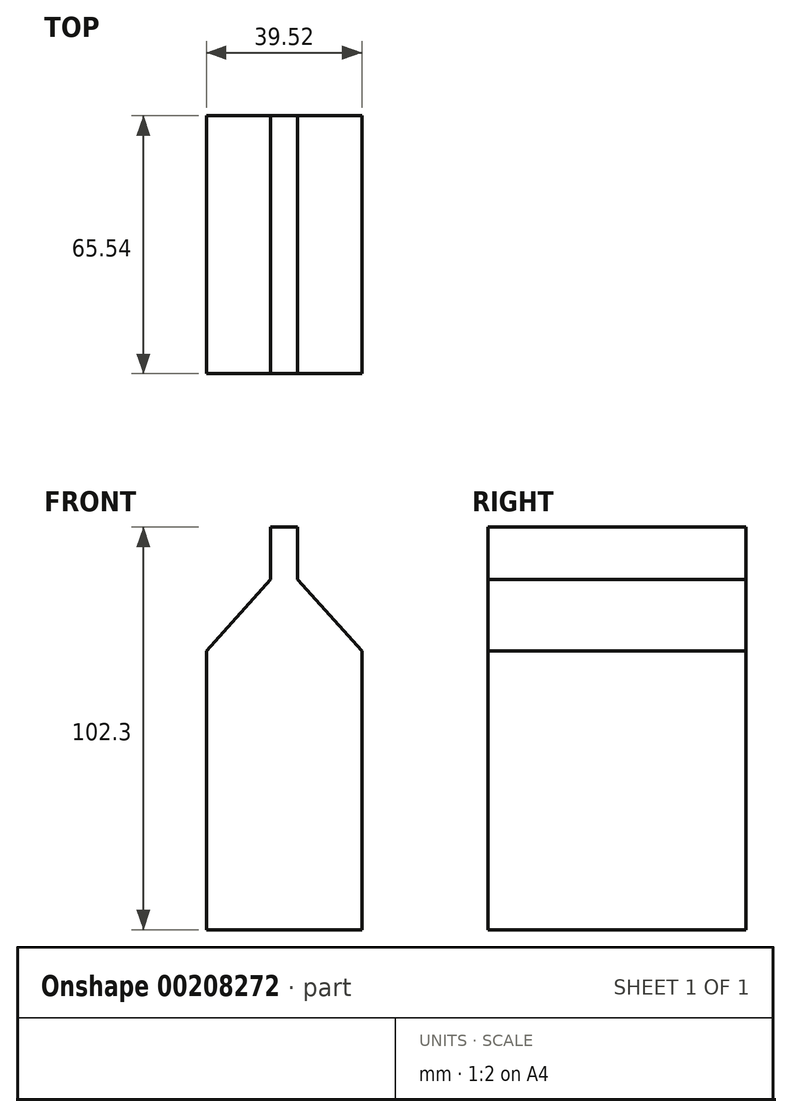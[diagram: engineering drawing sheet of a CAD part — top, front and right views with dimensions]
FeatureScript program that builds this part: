
annotation { "Feature Type Name" : "Feature", "Feature Type Description" : "" }
export const myFeature = defineFeature(function(context is Context, id is Id, definition is map)
    precondition{}
    {
        {
            var Q0;
            Q0=qCreatedBy(makeId("Front.planeOp"),FACE);
            var sketch = newSketch(context, id + "F0", { "sketchPlane" : qUnion([Q0])});
            skLineSegment(sketch, "E0.top", {"start": v(-19.76, -36.88) * mm, "end": v(19.76, -36.88) * mm});
            skLineSegment(sketch, "E0.left", {"start": v(-19.76, 33.96) * mm, "end": v(-19.76, -36.88) * mm});
            skLineSegment(sketch, "E0.right", {"start": v(19.76, 33.96) * mm, "end": v(19.76, -36.88) * mm});
            skPoint(sketch, "E0.middle", {"position": v(0, -1.46) * mm});
            skLineSegment(sketch, "E1", {"start": v(19.76, 33.96) * mm, "end": v(3.43, 52.12) * mm});
            skLineSegment(sketch, "E2", {"start": v(3.43, 52.12) * mm, "end": v(3.43, 65.42) * mm});
            skLineSegment(sketch, "E3", {"start": v(3.43, 65.42) * mm, "end": v(0, 65.42) * mm});
            skLineSegment(sketch, "E4.MirrorCS", {"start": v(-3.43, 65.42) * mm, "end": v(0, 65.42) * mm});
            skLineSegment(sketch, "E5.MirrorCS", {"start": v(-3.43, 52.12) * mm, "end": v(-3.43, 65.42) * mm});
            skLineSegment(sketch, "E6.MirrorCS", {"start": v(-19.76, 33.96) * mm, "end": v(-3.43, 52.12) * mm});
            skSolve(sketch);
        }
        {
            var Q0;
            Q0=makeQuery(id+"F0.imprint","IMPRINT",FACE,{"disambiguationData":[TD([[makeQuery(id+"F0.imprint","IMPRINT",EDGE,{"derivedFrom":sQuery(id+"F0.wireOp",EDGE,"E0.top")}),1.0]])]});
            extrude(context, id + "F1", {"entities" : qUnion([Q0]), "endBound" : BoundingType.SYMMETRIC, "depth" : 65.53 * mm});
        }
    });
